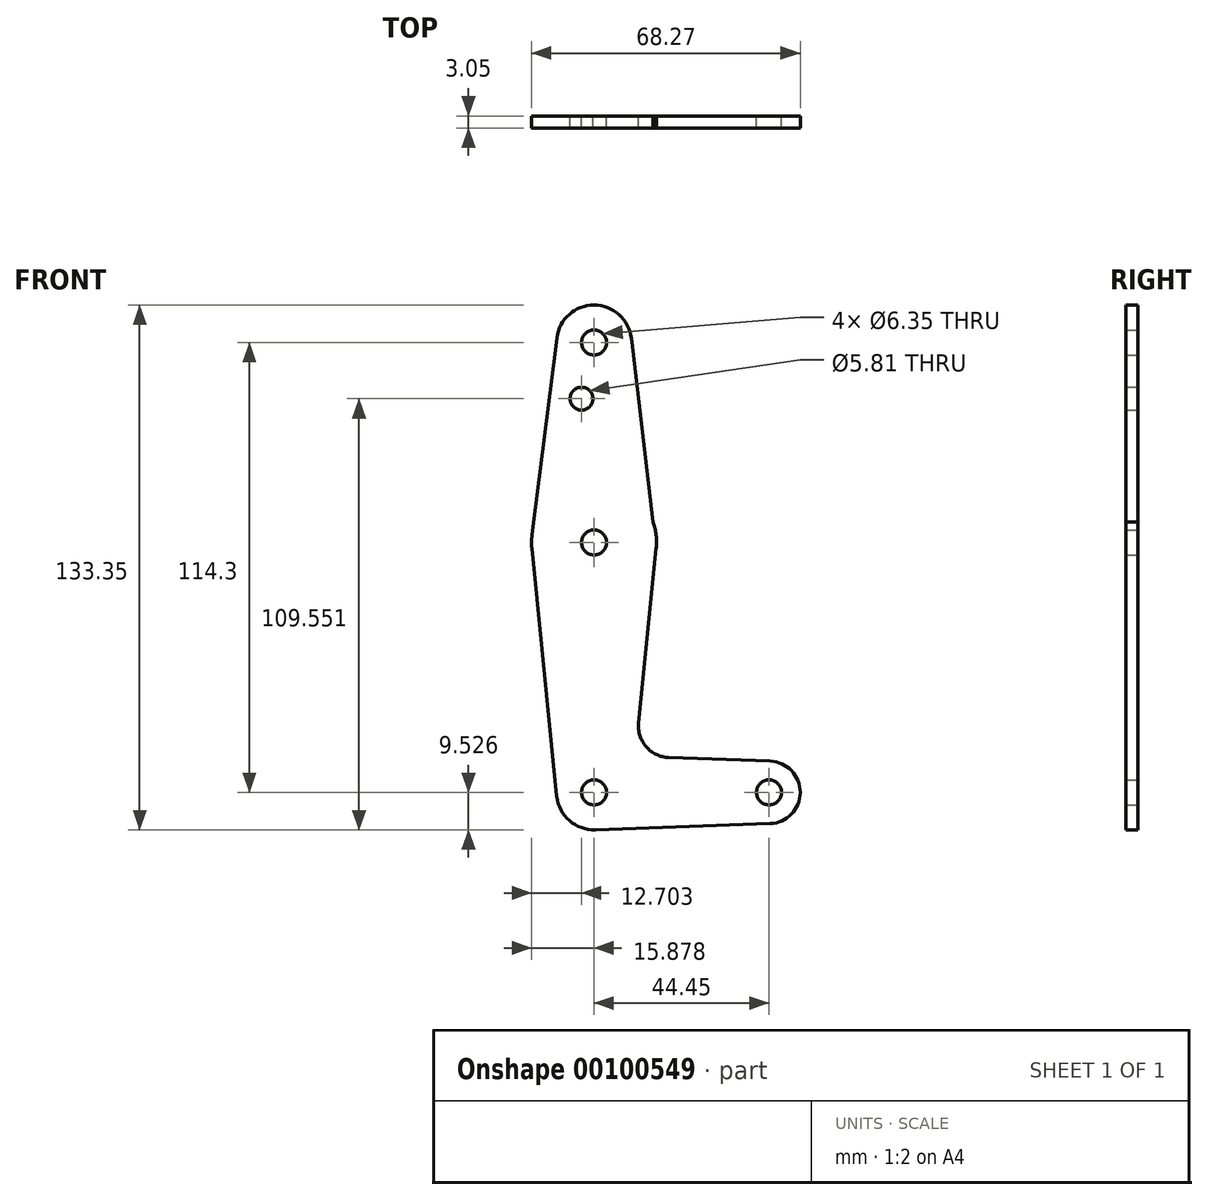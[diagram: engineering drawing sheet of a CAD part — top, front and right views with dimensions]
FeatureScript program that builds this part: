
annotation { "Feature Type Name" : "Feature", "Feature Type Description" : "" }
export const myFeature = defineFeature(function(context is Context, id is Id, definition is map)
    precondition{}
    {
        {
            var Q0;
            Q0=qCreatedBy(makeId("Front.planeOp"),FACE);
            var sketch = newSketch(context, id + "F0", { "sketchPlane" : qUnion([Q0])});
            skCircle(sketch, "E0", {"center": v(-69.7, 71.04) * mm, "radius": 9.53 * mm});
            skCircle(sketch, "E1", {"center": v(-69.7, -43.26) * mm, "radius": 9.53 * mm});
            skCircle(sketch, "E2", {"center": v(-25.24, -43.26) * mm, "radius": 7.94 * mm});
            skCircle(sketch, "E3", {"center": v(-69.7, 20.24) * mm, "radius": 15.88 * mm});
            skLineSegment(sketch, "E4", {"start": v(-79.14, 72.23) * mm, "end": v(-85.44, 22.22) * mm});
            skLineSegment(sketch, "E5", {"start": v(-60.23, 72.16) * mm, "end": v(-53.9, 18.65) * mm});
            skLineSegment(sketch, "E6", {"start": v(-53.9, 18.65) * mm, "end": v(-58.35, -25.67) * mm});
            skLineSegment(sketch, "E7", {"start": v(-69.35, -52.78) * mm, "end": v(-24.96, -51.2) * mm});
            skLineSegment(sketch, "E8", {"start": v(-50.72, -34.41) * mm, "end": v(-24.96, -35.33) * mm});
            skArc(sketch, "E9.filletArc", {"start": v(-58.35, -25.67) * mm, "mid": v(-56.43, -31.7) * mm, "end": v(-50.72, -34.41) * mm});
            skCircle(sketch, "E10", {"center": v(-72.87, 56.76) * mm, "radius": 2.9 * mm});
            skLineSegment(sketch, "E11", {"start": v(-85.49, 18.65) * mm, "end": v(-79.17, -44.22) * mm});
            skLineSegment(sketch, "E12", {"start": v(-69.7, 71.04) * mm, "end": v(-69.7, -43.26) * mm, "construction": true});
            skLineSegment(sketch, "E13", {"start": v(-69.7, -43.26) * mm, "end": v(-25.24, -43.26) * mm, "construction": true});
            skCircle(sketch, "E14", {"center": v(-69.7, 71.04) * mm, "radius": 3.18 * mm});
            skCircle(sketch, "E15", {"center": v(-69.7, 20.24) * mm, "radius": 3.18 * mm});
            skCircle(sketch, "E16", {"center": v(-69.7, -43.26) * mm, "radius": 3.18 * mm});
            skCircle(sketch, "E17", {"center": v(-25.24, -43.26) * mm, "radius": 3.18 * mm});
            skSolve(sketch);
        }
        {
            var Q0;
            Q0 = qSketchRegion(id + "F0", true);
            extrude(context, id + "F1", {"entities" : qUnion([Q0]), "depth" : 3.05 * mm});
        }
    });
